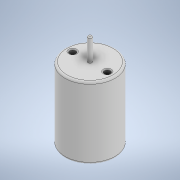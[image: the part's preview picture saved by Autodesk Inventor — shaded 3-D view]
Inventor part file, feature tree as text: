
AUTODESK INVENTOR PART (.ipt)
format: ipt  version: 2020.2 (Build 242310000, 310)  size: 144,384 bytes
history: native  units: mm
features: extrude x3, sketch x3, thread x2, fillet x1
ambient origin geometry x8: Origin, YZ Plane, XZ Plane, XY Plane, X Axis, Y Axis, Z Axis, Center Point
bodies: Solid1 (feature_tree)
feature tree (9):
  extrude  "Extrusion1"  Depth=35.2mm TaperAngle=0.0deg
  extrude  "Extrusion2"  Depth=11.0mm TaperAngle=0.0deg
  extrude  "Extrusion3"  Depth=0.5mm
  thread  "Thread1"  [1 undecoded]
  thread  "Thread2"  [1 undecoded]
  fillet  "Fillet1"  Radius=17.0mm
  sketch  "Sketch2"  dims[d1=24.6mm d2=35.2mm d3=0.0mm]
  sketch  "Sketch3"  dims[d4=2.0mm d5=11.0mm d6=0.0mm]
  sketch  "Sketch4"  dims[d7=3.0mm d9=8.5mm d11=20.0mm d13=360.0deg d15=17.0mm d16=0.0mm d17=17.0mm d18=0.0mm d19=17.0mm d20=0.0mm d21=1.0mm d22=0.5mm]
note: 2 required parameter values undecoded (feature->parameter linkage not recoverable at this tier; creation-order binding heuristic only, values carry confidence <= 0.55)
